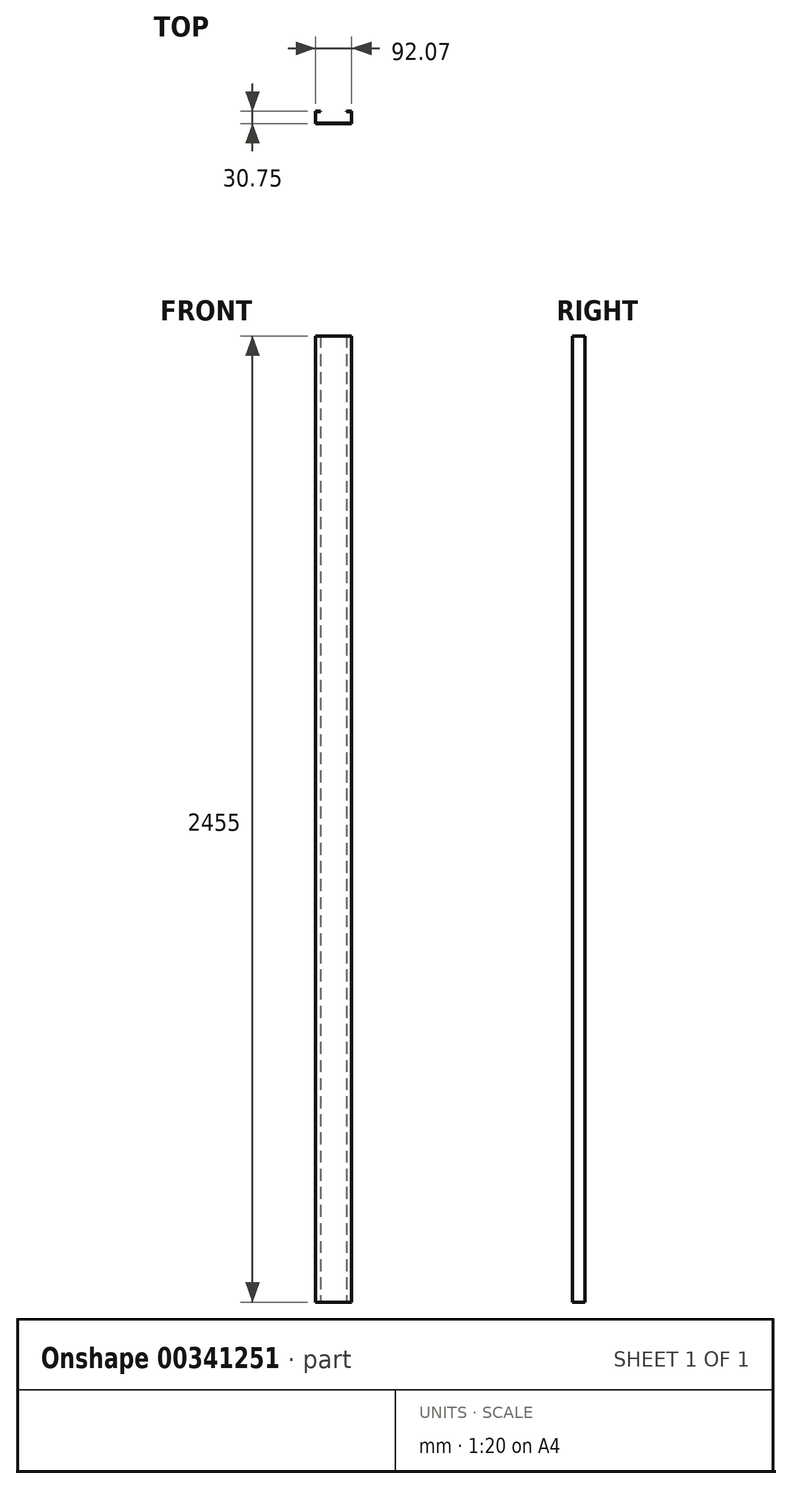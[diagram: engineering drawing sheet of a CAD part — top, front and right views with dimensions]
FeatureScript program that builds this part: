
annotation { "Feature Type Name" : "Feature", "Feature Type Description" : "" }
export const myFeature = defineFeature(function(context is Context, id is Id, definition is map)
    precondition{}
    {
        {
            var Q0;
            Q0=qCreatedBy(makeId("Top.planeOp"),FACE);
            var sketch = newSketch(context, id + "F0", { "sketchPlane" : qUnion([Q0])});
            skLineSegment(sketch, "E0", {"start": v(-91.26, 0) * mm, "end": v(-0.1, 0) * mm});
            skLineSegment(sketch, "E1", {"start": v(-0.1, 0) * mm, "end": v(-0.1, 29.84) * mm});
            skLineSegment(sketch, "E2", {"start": v(-0.1, 29.84) * mm, "end": v(-12.34, 29.84) * mm});
            skLineSegment(sketch, "E3", {"start": v(-91.26, 0) * mm, "end": v(-91.26, 29.84) * mm});
            skLineSegment(sketch, "E4", {"start": v(-91.26, 29.84) * mm, "end": v(-79.01, 29.84) * mm});
            skLineSegment(sketch, "E5.0", {"start": v(-91.71, 30.3) * mm, "end": v(-79.01, 30.3) * mm});
            skLineSegment(sketch, "E5.1", {"start": v(0.36, 30.3) * mm, "end": v(-12.34, 30.3) * mm});
            skLineSegment(sketch, "E5.2", {"start": v(0.36, -0.45) * mm, "end": v(0.36, 30.3) * mm});
            skLineSegment(sketch, "E5.3", {"start": v(-91.71, -0.45) * mm, "end": v(0.36, -0.45) * mm});
            skLineSegment(sketch, "E5.4", {"start": v(-91.71, -0.45) * mm, "end": v(-91.71, 30.3) * mm});
            skLineSegment(sketch, "E6", {"start": v(-79.01, 29.84) * mm, "end": v(-79.01, 30.3) * mm});
            skLineSegment(sketch, "E7", {"start": v(-12.34, 29.84) * mm, "end": v(-12.34, 30.3) * mm});
            skSolve(sketch);
        }
        {
            var Q0;
            Q0=makeQuery(id+"F0.imprint","IMPRINT",FACE,{"disambiguationData":[TD([[makeQuery(id+"F0.imprint","IMPRINT",EDGE,{"derivedFrom":sQuery(id+"F0.wireOp",EDGE,"E0")}),-1.0]])]});
            extrude(context, id + "F1", {"entities" : qUnion([Q0]), "depth" : 2455 * mm});
        }
    });
